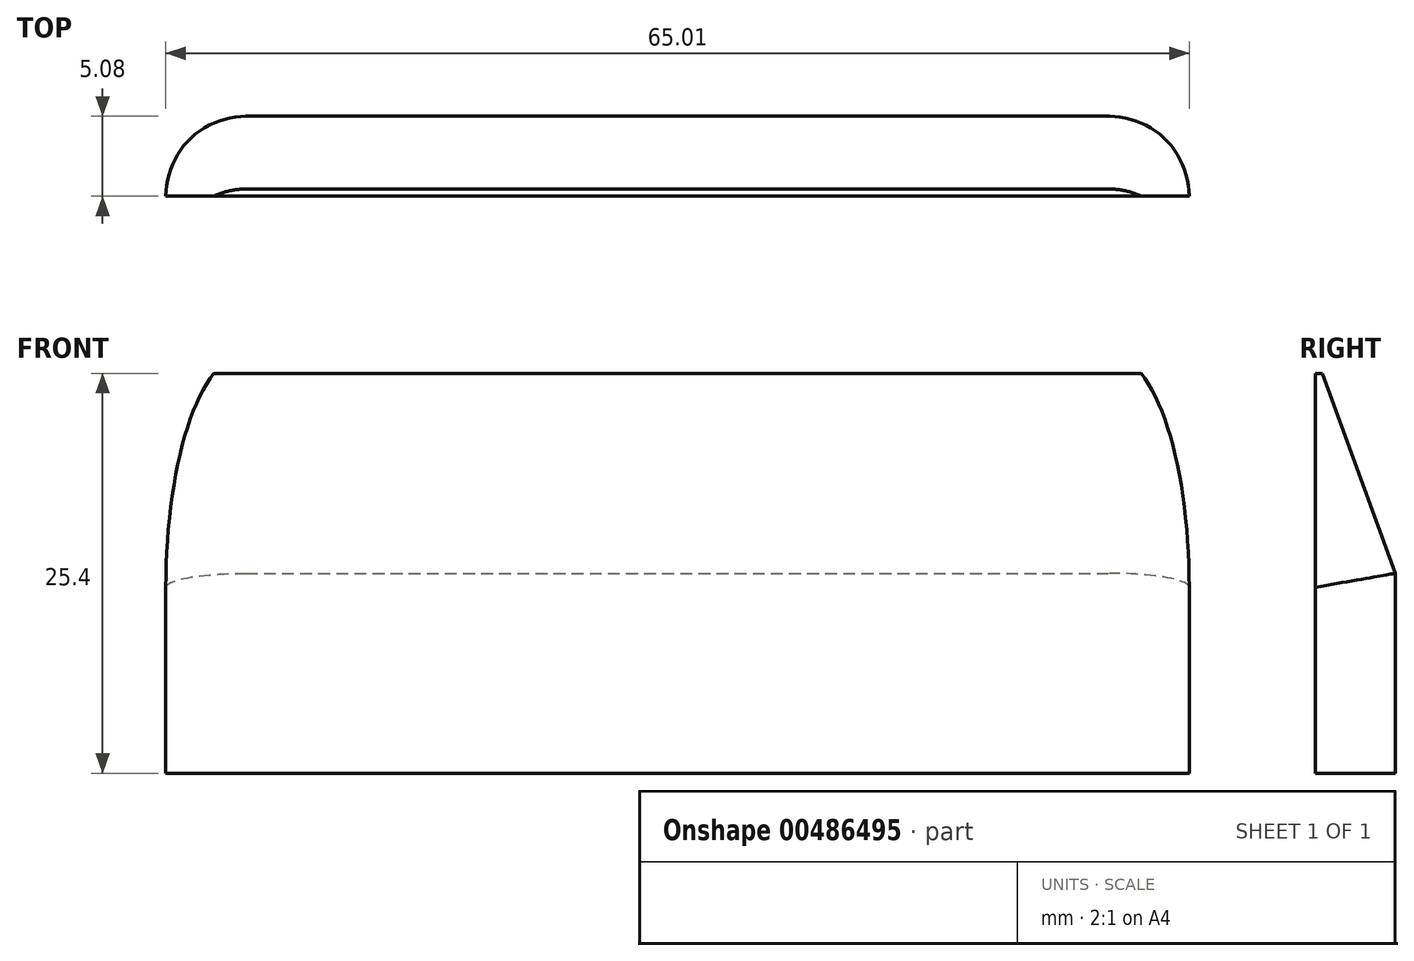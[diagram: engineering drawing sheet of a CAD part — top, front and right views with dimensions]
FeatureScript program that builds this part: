
annotation { "Feature Type Name" : "Feature", "Feature Type Description" : "" }
export const myFeature = defineFeature(function(context is Context, id is Id, definition is map)
    precondition{}
    {
        {
            var Q0;
            Q0=qCreatedBy(makeId("Top.planeOp"),FACE);
            var sketch = newSketch(context, id + "F0", { "sketchPlane" : qUnion([Q0])});
            skLineSegment(sketch, "E0.bottom", {"start": v(-43.6, 0) * mm, "end": v(21.4, 0) * mm});
            skLineSegment(sketch, "E0.top", {"start": v(-43.6, 5.08) * mm, "end": v(21.4, 5.08) * mm});
            skLineSegment(sketch, "E0.left", {"start": v(-43.6, 0) * mm, "end": v(-43.6, 5.08) * mm});
            skLineSegment(sketch, "E0.right", {"start": v(21.4, 0) * mm, "end": v(21.4, 5.08) * mm});
            skSolve(sketch);
        }
        {
            var Q0;
            Q0 = qSketchRegion(id + "F0", true);
            extrude(context, id + "F1", {"entities" : qUnion([Q0]), "depth" : 25.4 * mm});
        }
        {
            var Q0;
            Q0=makeQuery(id+"F1.opExtrude","CAP_EDGE",EDGE,{"disambiguationData":[OSD([sQuery(id+"F0.wireOp",EDGE,"E0.top")])],"isStart":false});
            chamfer(context, id + "F2", {"entities" : qUnion([Q0]), "chamferType" : ChamferType.OFFSET_ANGLE, "width" : 12.7 * mm, "oppositeDirection" : false, "angle" : 20 * degree, "tangentPropagation" : true});
        }
        {
            var Q0;
            Q0=makeQuery(id+"F2.opChamfer","BLEND_EDGE",EDGE,{"blendedFrom":[makeQuery(id+"F1.opExtrude","CAP_EDGE",EDGE,{"disambiguationData":[OSD([sQuery(id+"F0.wireOp",EDGE,"E0.top")])],"isStart":false}),makeQuery(id+"F1.opExtrude","SWEPT_FACE",FACE,{"disambiguationData":[OSD([sQuery(id+"F0.wireOp",EDGE,"E0.right")])]})],"blendedInto":[makeQuery(id+"F1.opExtrude","SWEPT_FACE",FACE,{"disambiguationData":[OSD([sQuery(id+"F0.wireOp",EDGE,"E0.right")])]})]});
            var Q1;
            Q1=makeQuery(id+"F1.opExtrude","SWEPT_EDGE",EDGE,{"disambiguationData":[OSD([sQuery(id+"F0.wireOp",EDGE,"E0.top"),sQuery(id+"F0.wireOp",EDGE,"E0.right")])]});
            var Q2;
            Q2=makeQuery(id+"F1.opExtrude","SWEPT_EDGE",EDGE,{"disambiguationData":[OSD([sQuery(id+"F0.wireOp",EDGE,"E0.top"),sQuery(id+"F0.wireOp",EDGE,"E0.left")])]});
            var Q3;
            Q3=makeQuery(id+"F2.opChamfer","BLEND_EDGE",EDGE,{"blendedFrom":[makeQuery(id+"F1.opExtrude","CAP_EDGE",EDGE,{"disambiguationData":[OSD([sQuery(id+"F0.wireOp",EDGE,"E0.top")])],"isStart":false}),makeQuery(id+"F1.opExtrude","SWEPT_FACE",FACE,{"disambiguationData":[OSD([sQuery(id+"F0.wireOp",EDGE,"E0.left")])]})],"blendedInto":[makeQuery(id+"F1.opExtrude","SWEPT_FACE",FACE,{"disambiguationData":[OSD([sQuery(id+"F0.wireOp",EDGE,"E0.left")])]})]});
            fillet(context, id + "F3", {"entities" : qUnion([Q0, Q1, Q2, Q3]), "radius" : 5.08 * mm, "tangentPropagation" : true, "allowEdgeOverflow" : false});
        }
    });
